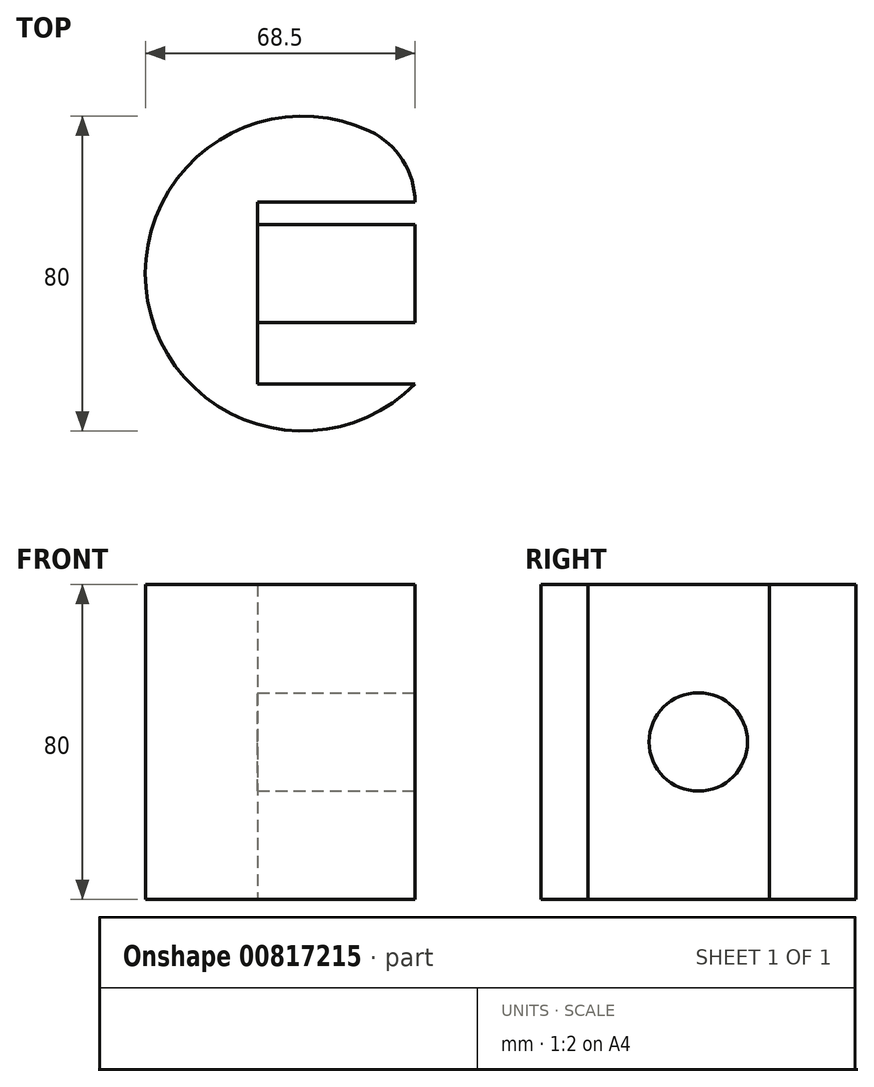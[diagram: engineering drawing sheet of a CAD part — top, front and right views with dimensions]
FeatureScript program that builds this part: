
annotation { "Feature Type Name" : "Feature", "Feature Type Description" : "" }
export const myFeature = defineFeature(function(context is Context, id is Id, definition is map)
    precondition{}
    {
        {
            var Q0;
            Q0=qCreatedBy(makeId("Top.planeOp"),FACE);
            var sketch = newSketch(context, id + "F0", { "sketchPlane" : qUnion([Q0])});
            skArc(sketch, "E0", {"start": v(17, 36.2) * mm, "mid": v(-39.38, -7.04) * mm, "end": v(28.5, -28.06) * mm});
            skLineSegment(sketch, "E1", {"start": v(28.5, 18.1) * mm, "end": v(28.5, -28.06) * mm});
            skPoint(sketch, "E2.visualSharp", {"position": v(28.5, 28.06) * mm});
            skArc(sketch, "E2.filletArc", {"start": v(28.5, 18.1) * mm, "mid": v(25.39, 28.82) * mm, "end": v(17, 36.2) * mm});
            skSolve(sketch);
        }
        {
            var Q0;
            Q0 = qSketchRegion(id + "F0", true);
            extrude(context, id + "F1", {"entities" : qUnion([Q0]), "depth" : 80 * mm, "offsetDistance" : 25 * mm});
        }
        {
            var Q0;
            Q0=makeQuery(id+"F1.opExtrude","SWEPT_FACE",FACE,{"disambiguationData":[OSD([sQuery(id+"F0.wireOp",EDGE,"E1")])]});
            var sketch = newSketch(context, id + "F2", { "sketchPlane" : qUnion([Q0])});
            skLineSegment(sketch, "E3", {"start": v(0, 80) * mm, "end": v(0, 0) * mm});
            skCircle(sketch, "E4", {"center": v(0, 40) * mm, "radius": 12.5 * mm});
            skSolve(sketch);
        }
        {
            var Q0;
            {var subQ0=sQuery(id+"F2.wireOp",EDGE,"E4");var subQ1=sQuery(id+"F2.wireOp",EDGE,"E3");var subQ2=makeQuery(id+"F2.imprint","INTERSECT",VERTEX,{"disambiguationData":[OD(0.0)],"derivedFrom":[subQ1,subQ0]});Q0=makeQuery(id+"F2.imprint","IMPRINT",FACE,{"disambiguationData":[TD([[makeQuery(id+"F2.imprint","IMPRINT",EDGE,{"disambiguationData":[TD([[subQ2,-1.0]])],"derivedFrom":subQ1}),1.0]])]});}
            var Q1;
            {var subQ0=sQuery(id+"F2.wireOp",EDGE,"E4");var subQ1=sQuery(id+"F2.wireOp",EDGE,"E3");var subQ2=makeQuery(id+"F2.imprint","INTERSECT",VERTEX,{"disambiguationData":[OD(0.0)],"derivedFrom":[subQ1,subQ0]});Q1=makeQuery(id+"F2.imprint","IMPRINT",FACE,{"disambiguationData":[TD([[makeQuery(id+"F2.imprint","IMPRINT",EDGE,{"disambiguationData":[TD([[subQ2,-1.0]])],"derivedFrom":subQ1}),-1.0]])]});}
            extrude(context, id + "F3", {"entities" : qUnion([Q0, Q1]), "operationType" : NewBodyOperationType.REMOVE, "oppositeDirection" : true, "depth" : 40 * mm, "offsetDistance" : 25 * mm});
        }
    });
